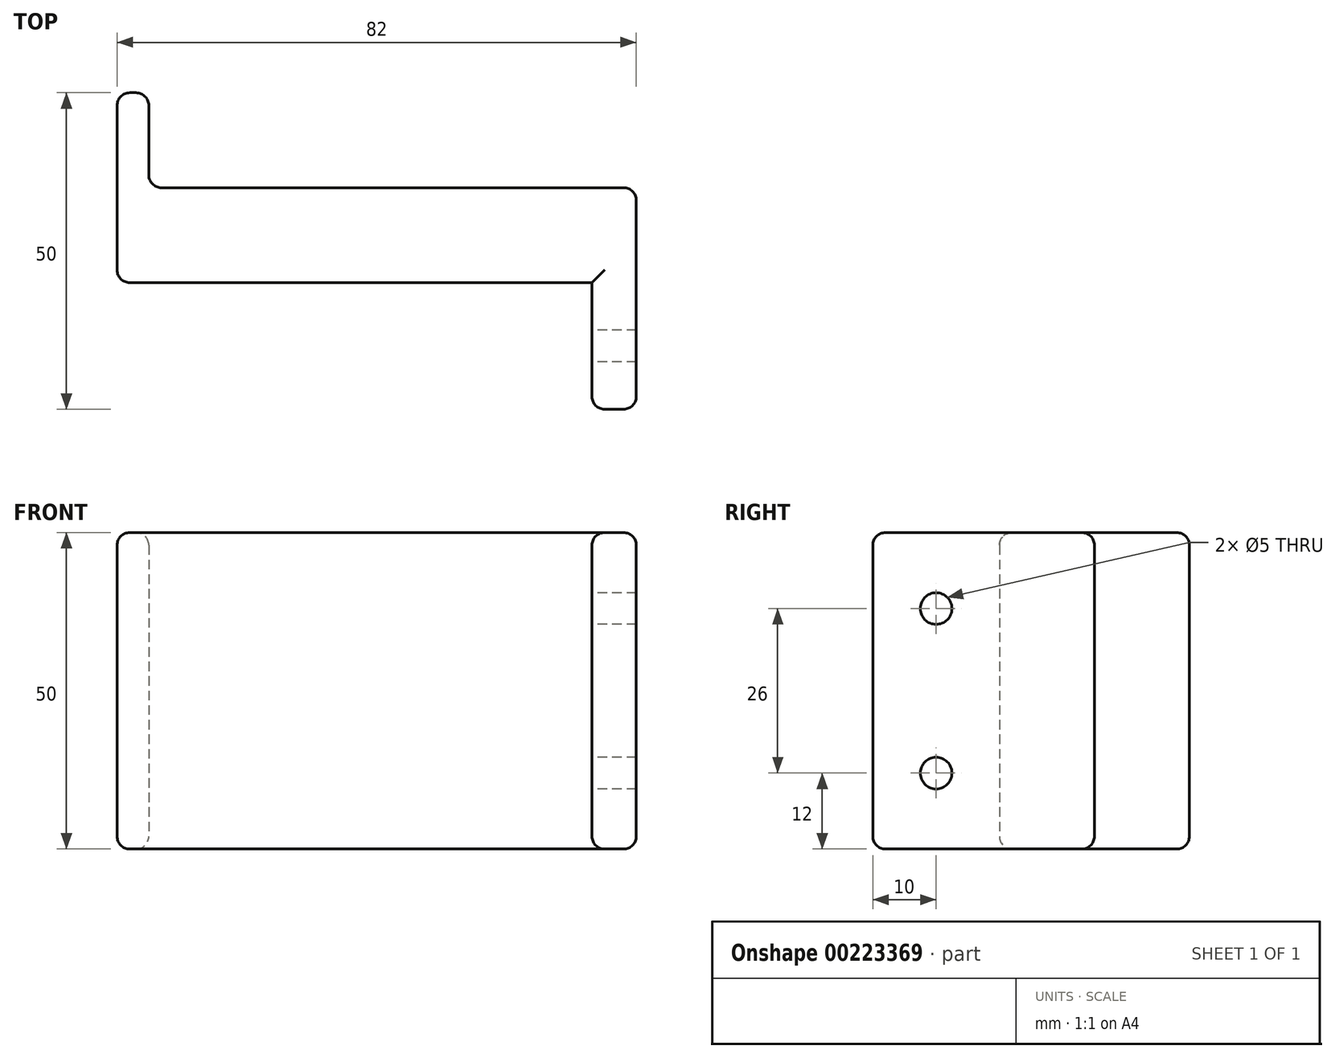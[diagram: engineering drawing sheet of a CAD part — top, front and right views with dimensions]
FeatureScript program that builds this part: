
annotation { "Feature Type Name" : "Feature", "Feature Type Description" : "" }
export const myFeature = defineFeature(function(context is Context, id is Id, definition is map)
    precondition{}
    {
        {
            var Q0;
            Q0=qCreatedBy(makeId("Top.planeOp"),FACE);
            var sketch = newSketch(context, id + "F0", { "sketchPlane" : qUnion([Q0])});
            skLineSegment(sketch, "E0.bottom", {"start": v(34, -15) * mm, "end": v(-41, -15) * mm});
            skLineSegment(sketch, "E0.top", {"start": v(-36, 15) * mm, "end": v(-41, 15) * mm});
            skLineSegment(sketch, "E0.right", {"start": v(-41, -15) * mm, "end": v(-41, 15) * mm});
            skPoint(sketch, "E0.middle", {"position": v(0, 0) * mm});
            skLineSegment(sketch, "E1", {"start": v(41, 0) * mm, "end": v(-36, 0) * mm});
            skPoint(sketch, "E1.endSnap0", {"position": v(41, 0) * mm});
            skLineSegment(sketch, "E2", {"start": v(-36, 0) * mm, "end": v(-36, 15) * mm});
            skPoint(sketch, "E3.orphan", {"position": v(41, 15) * mm});
            skLineSegment(sketch, "E4", {"start": v(41, -15) * mm, "end": v(41, -35) * mm});
            skPoint(sketch, "E5.end.orphan", {"position": v(41, 35) * mm});
            skPoint(sketch, "E6.orphan", {"position": v(46, 35) * mm});
            skLineSegment(sketch, "E7", {"start": v(34, -15) * mm, "end": v(34, -35) * mm});
            skLineSegment(sketch, "E8", {"start": v(34, -35) * mm, "end": v(41, -35) * mm});
            skLineSegment(sketch, "E9", {"start": v(41, 0) * mm, "end": v(41, -15) * mm});
            skPoint(sketch, "E10.end.orphan", {"position": v(46, 0) * mm});
            skPoint(sketch, "E11.end.orphan", {"position": v(46, -35) * mm});
            skSolve(sketch);
        }
        {
            var Q0;
            Q0=makeQuery(id+"F0.imprint","IMPRINT",FACE,{"disambiguationData":[TD([[makeQuery(id+"F0.imprint","IMPRINT",EDGE,{"derivedFrom":sQuery(id+"F0.wireOp",EDGE,"E0.bottom")}),-1.0]])]});
            extrude(context, id + "F1", {"entities" : qUnion([Q0]), "depth" : 50 * mm});
        }
        {
            var Q0;
            Q0=makeQuery(id+"F1.opExtrude","SWEPT_FACE",FACE,{"disambiguationData":[OSD([sQuery(id+"F0.wireOp",EDGE,"E7")])]});
            var sketch = newSketch(context, id + "F2", { "sketchPlane" : qUnion([Q0])});
            skLineSegment(sketch, "E12", {"start": v(35, 0) * mm, "end": v(35, 12) * mm});
            skLineSegment(sketch, "E13", {"start": v(35, 50) * mm, "end": v(35, 38) * mm});
            skLineSegment(sketch, "E14", {"start": v(35, 38) * mm, "end": v(25, 38) * mm});
            skLineSegment(sketch, "E15", {"start": v(35, 12) * mm, "end": v(25, 12) * mm});
            skCircle(sketch, "E16", {"center": v(25, 12) * mm, "radius": 2.5 * mm});
            skCircle(sketch, "E17", {"center": v(25, 38) * mm, "radius": 2.5 * mm});
            skSolve(sketch);
        }
        {
            var Q0;
            Q0=makeQuery(id+"F2.imprint","IMPRINT",FACE,{"disambiguationData":[TD([[makeQuery(id+"F2.imprint","IMPRINT",EDGE,{"derivedFrom":sQuery(id+"F2.wireOp",EDGE,"E16")}),1.0]])]});
            var Q1;
            Q1=makeQuery(id+"F2.imprint","IMPRINT",FACE,{"disambiguationData":[TD([[makeQuery(id+"F2.imprint","IMPRINT",EDGE,{"derivedFrom":sQuery(id+"F2.wireOp",EDGE,"E17")}),1.0]])]});
            extrude(context, id + "F3", {"entities" : qUnion([Q0, Q1]), "operationType" : NewBodyOperationType.REMOVE, "oppositeDirection" : true, "depth" : 25 * mm});
        }
        {
            var Q0;
            Q0=makeQuery(id+"F1.opExtrude","CAP_FACE",FACE,{"disambiguationData":[OSD([sQuery(id+"F0.wireOp",EDGE,"E0.bottom"),sQuery(id+"F0.wireOp",EDGE,"E0.top"),sQuery(id+"F0.wireOp",EDGE,"E0.right"),sQuery(id+"F0.wireOp",EDGE,"E1"),sQuery(id+"F0.wireOp",EDGE,"E2"),sQuery(id+"F0.wireOp",EDGE,"E4"),sQuery(id+"F0.wireOp",EDGE,"E7"),sQuery(id+"F0.wireOp",EDGE,"E8"),sQuery(id+"F0.wireOp",EDGE,"E9")])],"isStart":false});
            var Q1;
            Q1=makeQuery(id+"F1.opExtrude","CAP_FACE",FACE,{"disambiguationData":[OSD([sQuery(id+"F0.wireOp",EDGE,"E0.bottom"),sQuery(id+"F0.wireOp",EDGE,"E0.top"),sQuery(id+"F0.wireOp",EDGE,"E0.right"),sQuery(id+"F0.wireOp",EDGE,"E1"),sQuery(id+"F0.wireOp",EDGE,"E2"),sQuery(id+"F0.wireOp",EDGE,"E4"),sQuery(id+"F0.wireOp",EDGE,"E7"),sQuery(id+"F0.wireOp",EDGE,"E8"),sQuery(id+"F0.wireOp",EDGE,"E9")])],"isStart":true});
            var Q2;
            Q2=makeQuery(id+"F1.opExtrude","SWEPT_EDGE",EDGE,{"disambiguationData":[OSD([sQuery(id+"F0.wireOp",EDGE,"E7"),sQuery(id+"F0.wireOp",EDGE,"E8")])]});
            var Q3;
            Q3=makeQuery(id+"F1.opExtrude","SWEPT_EDGE",EDGE,{"disambiguationData":[OSD([sQuery(id+"F0.wireOp",EDGE,"E0.bottom"),sQuery(id+"F0.wireOp",EDGE,"E0.right")])]});
            var Q4;
            Q4=makeQuery(id+"F1.opExtrude","SWEPT_EDGE",EDGE,{"disambiguationData":[OSD([sQuery(id+"F0.wireOp",EDGE,"E0.top"),sQuery(id+"F0.wireOp",EDGE,"E0.right")])]});
            var Q5;
            Q5=makeQuery(id+"F1.opExtrude","SWEPT_EDGE",EDGE,{"disambiguationData":[OSD([sQuery(id+"F0.wireOp",EDGE,"E0.top"),sQuery(id+"F0.wireOp",EDGE,"E2")])]});
            var Q6;
            Q6=makeQuery(id+"F1.opExtrude","SWEPT_EDGE",EDGE,{"disambiguationData":[OSD([sQuery(id+"F0.wireOp",EDGE,"E1"),sQuery(id+"F0.wireOp",EDGE,"E9")])]});
            var Q7;
            Q7=makeQuery(id+"F1.opExtrude","SWEPT_EDGE",EDGE,{"disambiguationData":[OSD([sQuery(id+"F0.wireOp",EDGE,"E1"),sQuery(id+"F0.wireOp",EDGE,"E2")])]});
            var Q8;
            Q8=makeQuery(id+"F1.opExtrude","SWEPT_EDGE",EDGE,{"disambiguationData":[OSD([sQuery(id+"F0.wireOp",EDGE,"E4"),sQuery(id+"F0.wireOp",EDGE,"E8")])]});
            fillet(context, id + "F4", {"entities" : qUnion([Q0, Q1, Q2, Q3, Q4, Q5, Q6, Q7, Q8]), "radius" : 2 * mm, "tangentPropagation" : true, "allowEdgeOverflow" : false});
        }
    });
